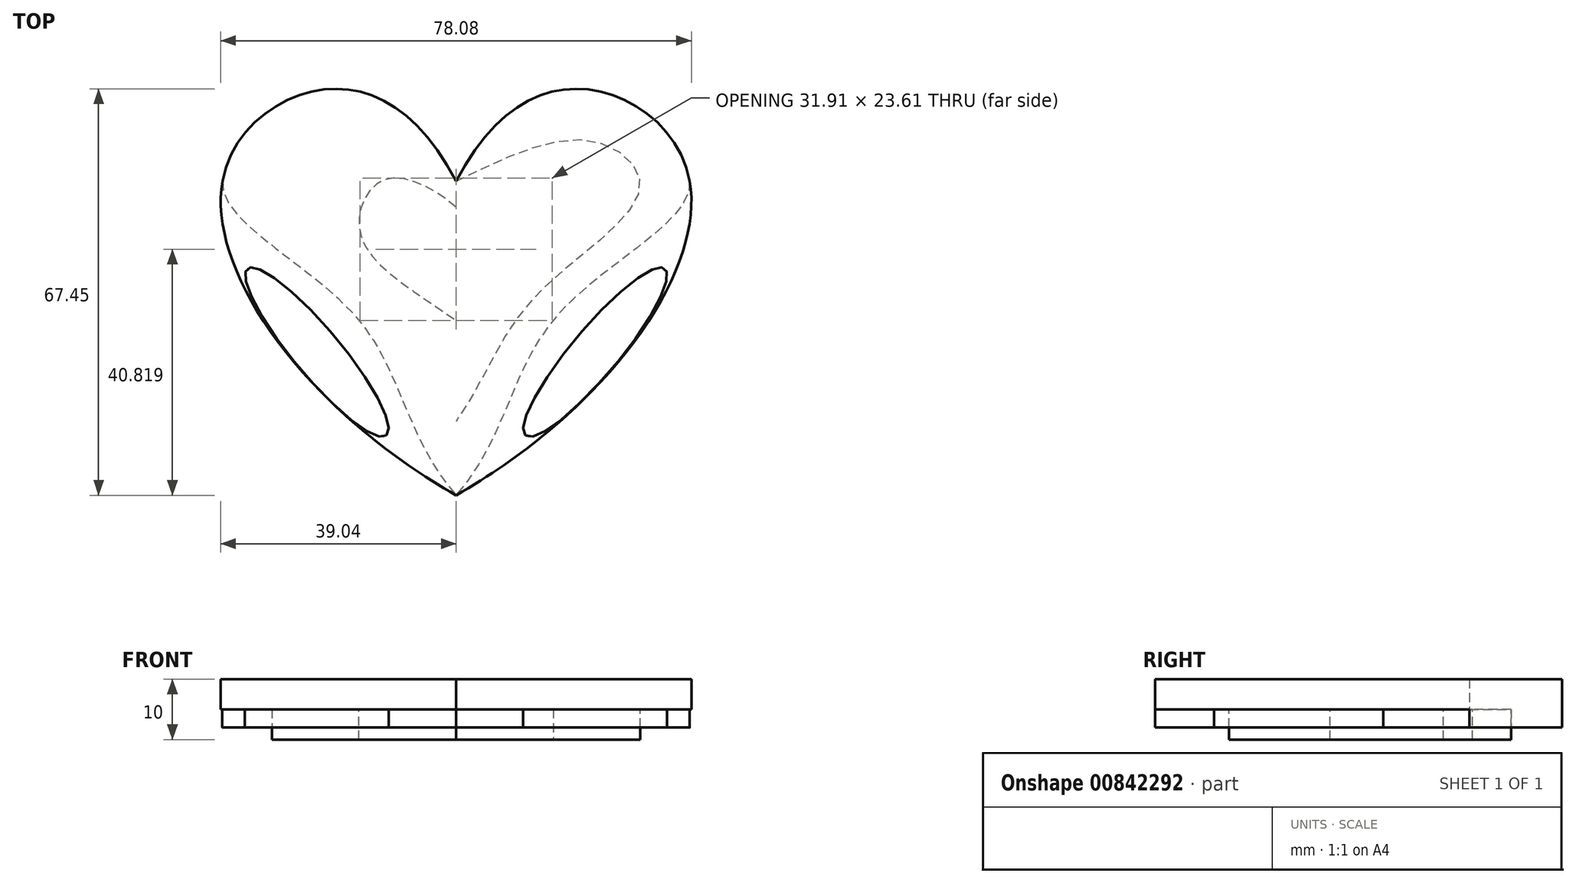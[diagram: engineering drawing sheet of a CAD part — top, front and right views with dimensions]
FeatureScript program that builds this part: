
annotation { "Feature Type Name" : "Feature", "Feature Type Description" : "" }
export const myFeature = defineFeature(function(context is Context, id is Id, definition is map)
    precondition{}
    {
        {
            var Q0;
            Q0=qCreatedBy(makeId("Top.planeOp"),FACE);
            var sketch = newSketch(context, id + "F0", { "sketchPlane" : qUnion([Q0])});
            skFitSpline(sketch, "E0", {"points": [v(0, 0) * mm, v(-21.78, 15.23) * mm, v(-38.75, 0) * mm, v(0, -52.1) * mm], "startDerivative": vector(-61.58, 117.99) * mm, "endDerivative": vector(173.73, -99.9) * mm});
            skFitSpline(sketch, "E1.MirrorCS", {"points": [v(0, 0) * mm, v(21.78, 15.23) * mm, v(38.75, 0) * mm, v(0, -52.1) * mm], "startDerivative": vector(61.58, 117.99) * mm, "endDerivative": vector(-173.73, -99.9) * mm});
            skFitSpline(sketch, "E2", {"points": [v(0, 0) * mm, v(-22.15, 6.75) * mm, v(-30.5, 0) * mm, v(-23.47, -10.1) * mm, v(-10.61, -22.06) * mm, v(0, -39.85) * mm], "startDerivative": vector(-101.95, 49.3) * mm, "endDerivative": vector(55, -77.97) * mm});
            skPoint(sketch, "E3", {"position": v(-25.47, -31.66) * mm});
            skFitSpline(sketch, "E4", {"points": [v(-38.75, 0) * mm, v(-16.95, -22.06) * mm, v(0, -52.1) * mm], "startDerivative": vector(-4.02, -40.81) * mm, "endDerivative": vector(50.77, -58.34) * mm});
            skEllipse(sketch, "E5", {"center": v(-23.08, -28.34) * mm, "majorRadius": 18.02 * mm, "minorRadius": 3.9 * mm, "majorAxis": v(0.64, -0.77)});
            skFitSpline(sketch, "E6", {"points": [v(0, -4.28) * mm, v(-12.38, 0) * mm, v(-15.9, -8.69) * mm, v(0, -23.1) * mm], "startDerivative": vector(-40.45, 34.58) * mm, "endDerivative": vector(57.5, -40.05) * mm});
            skFitSpline(sketch, "E7.MirrorCS", {"points": [v(0, 0) * mm, v(22.15, 6.75) * mm, v(30.5, 0) * mm, v(23.47, -10.1) * mm, v(10.61, -22.06) * mm, v(0, -39.85) * mm], "startDerivative": vector(101.95, 49.3) * mm, "endDerivative": vector(-55, -77.97) * mm});
            skFitSpline(sketch, "E8.MirrorCS", {"points": [v(0, -4.28) * mm, v(12.38, 0) * mm, v(15.9, -8.69) * mm, v(0, -23.1) * mm], "startDerivative": vector(40.45, 34.58) * mm, "endDerivative": vector(-57.5, -40.05) * mm});
            skFitSpline(sketch, "E9.MirrorCS", {"points": [v(38.75, 0) * mm, v(16.95, -22.06) * mm, v(0, -52.1) * mm], "startDerivative": vector(4.02, -40.81) * mm, "endDerivative": vector(-50.77, -58.34) * mm});
            skEllipse(sketch, "E10.MirrorC", {"center": v(23.08, -28.34) * mm, "majorRadius": 18.02 * mm, "minorRadius": 3.9 * mm, "majorAxis": v(-0.64, -0.77)});
            skSolve(sketch);
        }
        {
            var Q0;
            Q0 = qSketchRegion(id + "F0", true);
            var Q1;
            Q1=makeQuery(id+"F0.imprint","IMPRINT",FACE,{"disambiguationData":[TD([[makeQuery(id+"F0.imprint","IMPRINT",EDGE,{"derivedFrom":sQuery(id+"F0.wireOp",EDGE,"E6")}),1.0]])]});
            extrude(context, id + "F1", {"entities" : qUnion([Q0, Q1]), "depth" : 5 * mm, "offsetDistance" : 25 * mm});
        }
        {
            var Q0;
            {var subQ1=sQuery(id+"F0.wireOp",EDGE,"E2");Q0=makeQuery(id+"F0.imprint","IMPRINT",FACE,{"disambiguationData":[TD([[makeQuery(id+"F0.imprint","IMPRINT",EDGE,{"derivedFrom":subQ1}),-1.0]])]});}
            var Q1;
            Q1=makeQuery(id+"F0.imprint","IMPRINT",FACE,{"disambiguationData":[TD([[makeQuery(id+"F0.imprint","IMPRINT",EDGE,{"derivedFrom":sQuery(id+"F0.wireOp",EDGE,"E2")}),1.0]])]});
            var Q2;
            Q2=makeQuery(id+"F0.imprint","IMPRINT",FACE,{"disambiguationData":[TD([[makeQuery(id+"F0.imprint","IMPRINT",EDGE,{"derivedFrom":sQuery(id+"F0.wireOp",EDGE,"E6")}),1.0]])]});
            var Q3;
            Q3=makeQuery(id+"F0.imprint","IMPRINT",FACE,{"disambiguationData":[TD([[makeQuery(id+"F0.imprint","IMPRINT",EDGE,{"derivedFrom":sQuery(id+"F0.wireOp",EDGE,"E10.MirrorC")}),1.0]])]});
            var Q4;
            Q4=makeQuery(id+"F0.imprint","IMPRINT",FACE,{"disambiguationData":[TD([[makeQuery(id+"F0.imprint","IMPRINT",EDGE,{"derivedFrom":sQuery(id+"F0.wireOp",EDGE,"E5")}),1.0]])]});
            extrude(context, id + "F2", {"entities" : qUnion([Q0, Q1, Q2, Q3, Q4]), "operationType" : NewBodyOperationType.ADD, "oppositeDirection" : true, "depth" : 3 * mm, "offsetDistance" : 25 * mm});
        }
        {
            var Q0;
            Q0=makeQuery(id+"F0.imprint","IMPRINT",FACE,{"disambiguationData":[TD([[makeQuery(id+"F0.imprint","IMPRINT",EDGE,{"derivedFrom":sQuery(id+"F0.wireOp",EDGE,"E2")}),1.0]])]});
            var Q1;
            Q1=makeQuery(id+"Fjwj7ZbEGDsMpmW_1.opExtrude","CAP_FACE",FACE,{"disambiguationData":[OSD([sQuery(id+"F0.wireOp",EDGE,"E6"),sQuery(id+"F0.wireOp",EDGE,"E8.MirrorCS")])],"isStart":false});
            extrude(context, id + "F3", {"entities" : qUnion([Q0, Q1]), "oppositeDirection" : true, "depth" : 5 * mm, "offsetDistance" : 25 * mm});
        }
    });
